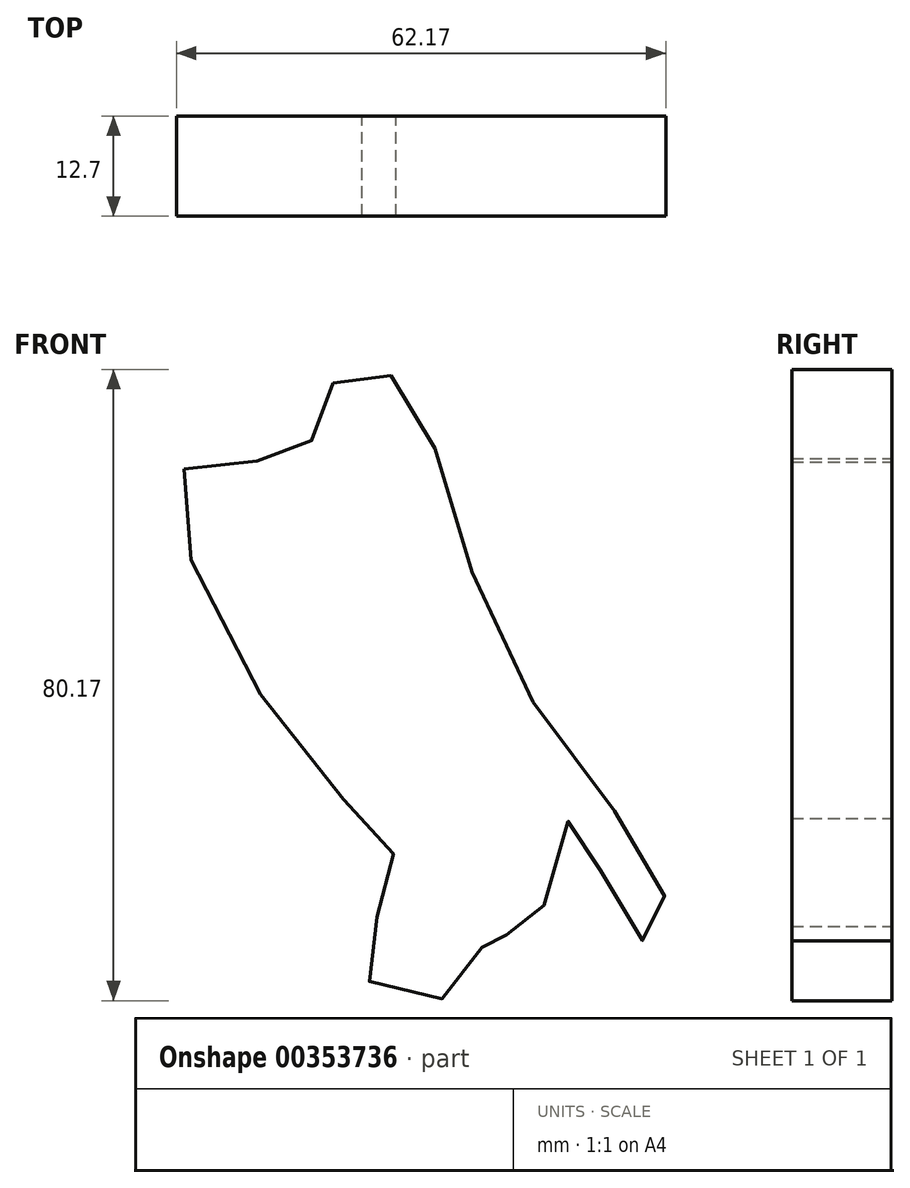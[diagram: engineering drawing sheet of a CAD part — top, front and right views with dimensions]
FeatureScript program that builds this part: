
annotation { "Feature Type Name" : "Feature", "Feature Type Description" : "" }
export const myFeature = defineFeature(function(context is Context, id is Id, definition is map)
    precondition{}
    {
        {
            var Q0;
            Q0=qCreatedBy(makeId("Front.planeOp"),FACE);
            var sketch = newSketch(context, id + "F0", { "sketchPlane" : qUnion([Q0])});
            skFitSpline(sketch, "E0", {"points": [v(-75.33, 59.6) * mm, v(-58, 20.65) * mm, v(-48.47, 8.42) * mm, v(-52.34, -4.68) * mm, v(-39.65, -6.25) * mm, v(-36.41, 1.48) * mm, v(-31.85, -0.19) * mm, v(-26.05, 15.2) * mm, v(-17.84, 0) * mm, v(-14.12, 3.78) * mm, v(-34.5, 36.04) * mm, v(-48.53, 71.12) * mm, v(-57.1, 69.6) * mm, v(-60.85, 61) * mm, v(-75.33, 59.6) * mm]});
            skSolve(sketch);
        }
        {
            var Q0;
            Q0=makeQuery(id+"F0.imprint","IMPRINT",FACE,{"disambiguationData":[TD([[makeQuery(id+"F0.imprint","IMPRINT",EDGE,{"derivedFrom":sQuery(id+"F0.wireOp",EDGE,"E0")}),1.0]])]});
            extrude(context, id + "F1", {"entities" : qUnion([Q0]), "depth" : 12.7 * mm});
        }
    });
